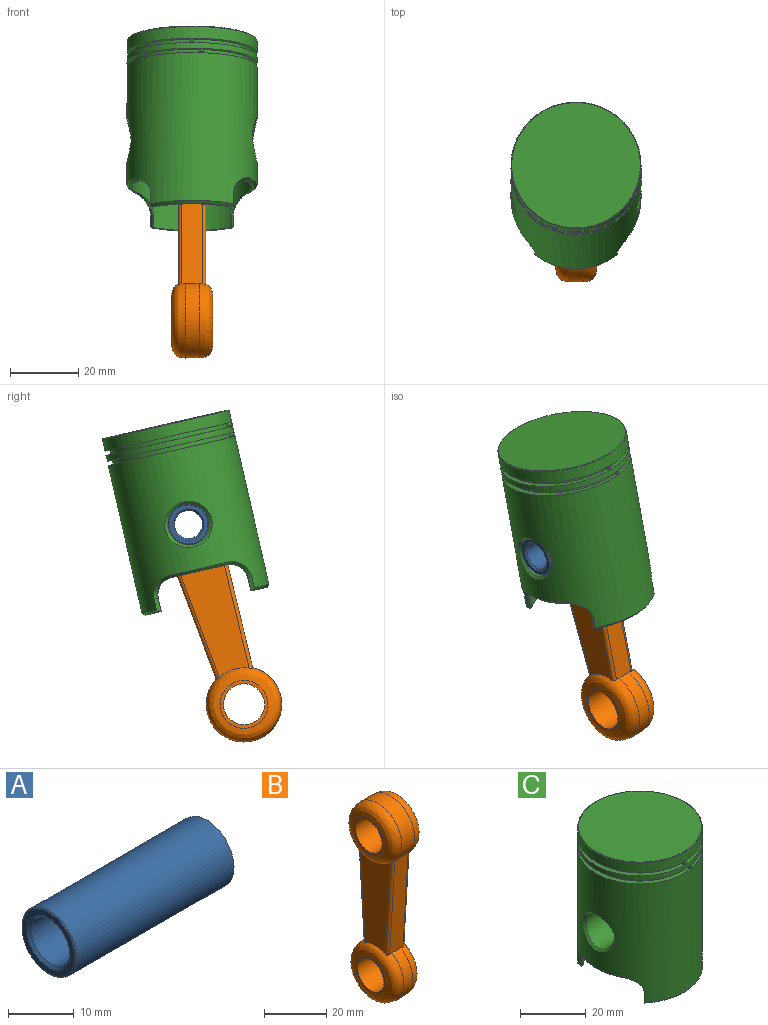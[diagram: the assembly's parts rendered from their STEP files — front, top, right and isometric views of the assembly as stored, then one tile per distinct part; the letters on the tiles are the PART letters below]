
ASSEMBLY  parts=3 mates=2
PART A: 6 faces, bbox 34x11.8x11.8 mm
  f0: cylinder r=4.1mm len=33.5mm, axis (1,0,0), area 863mm2, adj f2,f5
  f1: cylinder r=5.9mm len=33.8mm, axis (1,0,0), area 1253mm2, adj f2,f4
  f2: plane 11.8x11.8mm, normal (1,0,0), area 56.5mm2, adj f0,f1
  f3: plane 11.4x11.4mm, normal (-1,0,0), area 35.6mm2, adj f4,f5
  f4: cone r=5.9mm half-angle=45deg, axis (1,0,0), area 10.3mm2, adj f1,f3
  f5: cone r=4.6mm half-angle=45deg, axis (-1,0,0), area 19.3mm2, adj f0,f3
PART B: 21 faces, bbox 13.8x22x77 mm
  f0: cylinder r=6mm len=13.8mm, axis (1,0,0), area 520.2mm2, adj f2,f10
  f1: cylinder r=11mm len=22mm, axis (1,0,0), area 298.5mm2, adj f6,f7,f12,f13,f15
  f2: plane 14.01x14.01mm, normal (1,0,0), area 40.8mm2, adj f0,f15
  f3: cylinder r=11mm len=22mm, axis (1,0,0), area 229.8mm2, adj f6,f7,f14,f16
  f4: cylinder r=6mm len=12mm, axis (1,0,0), area 452.4mm2, adj f5,f9
  f5: plane 14.01x14.01mm, normal (1,0,0), area 40.8mm2, adj f4,f16
  f6: plane 37.97x6.04mm, normal (0,1,-0.06), area 227.7mm2, adj f1,f3,f12,f14,f15,f16,f18,f20
  f7: plane 37.97x6.04mm, normal (0,-1,-0.06), area 227.7mm2, adj f1,f3,f13,f14,f15,f16,f17,f19
  f8: plane 37.02x13.9mm, normal (1,0,0), area 392.3mm2, adj f15,f16,f19,f20
  f9: plane 14.01x14.01mm, normal (-1,0,0), area 40.9mm2, adj f4,f14
  f10: plane 14.01x14.01mm, normal (-1,0,0), area 40.8mm2, adj f0,f12
  f11: plane 37.02x13.9mm, normal (-1,0,0), area 392.3mm2, adj f12,f14,f17,f18
  f12: bspline ~21.99x21.98mm, area 374.1mm2, adj f1,f6,f10,f11,f13,f17,f18
  f13: bspline ~6.96x6.41mm, area 0mm2, adj f1,f7,f12
  f14: bspline ~21.99x21.98mm, area 369.7mm2, adj f3,f6,f7,f9,f11,f17,f18
  f15: bspline ~22x22mm, area 374.1mm2, adj f1,f2,f6,f7,f8,f19,f20
  f16: bspline ~22x22mm, area 369.7mm2, adj f3,f5,f6,f7,f8,f19,f20
  f17: cylinder r=1mm len=38.01mm, axis (0,0.06,-1), area 58.9mm2, adj f7,f11,f12,f14
  f18: cylinder r=1mm len=38.01mm, axis (0,0.06,1), area 58.9mm2, adj f6,f11,f12,f14
  f19: cylinder r=1mm len=38.01mm, axis (0,0.06,-1), area 58.9mm2, adj f7,f8,f15,f16
  f20: cylinder r=1mm len=38.01mm, axis (0,0.06,1), area 58.9mm2, adj f6,f8,f15,f16
PART C: 57 faces, bbox 38x38x53 mm
  f0: cylinder r=19mm len=38mm, axis (0,0,1), area 203.8mm2, adj f3,f7,f25
  f1: cylinder r=17.5mm len=35mm, axis (0,0,1), area 142.2mm2, adj f2,f3,f24
  f2: plane 38x38mm, normal (0,0,-1), area 171.9mm2, adj f1,f5,f24
  f3: plane 38x38mm, normal (0,0,1), area 172mm2, adj f0,f1
  f4: plane 37.6x37.6mm, normal (0,0,1), area 1110.4mm2, adj f52
  f5: cylinder r=19mm len=38mm, axis (0,0,1), area 418.6mm2, adj f2,f24,f52
  f6: cylinder r=17.5mm len=35mm, axis (0,0,1), area 142.1mm2, adj f7,f8,f25
  f7: plane 38x38mm, normal (0,0,-1), area 171.5mm2, adj f0,f6,f25
  f8: plane 38x38mm, normal (0,0,1), area 172mm2, adj f6,f23
  f9: plane 35x35mm, normal (0,0,-1), area 962.1mm2, adj f10
  f10: cylinder r=17.5mm len=43mm, axis (0,0,1), area 3596.7mm2, adj f9,f11,f12,f13,f14,f15,f16,f17
  f11: plane 23.72x4.9mm, normal (0,0,-1), area 20.3mm2, adj f10,f12,f22,f45,f47,f49
  f12: plane 4x0.41mm, normal (0,-1,0), area 1.6mm2, adj f10,f11,f13,f49
  f13: cylinder r=5mm len=5mm, axis (-1,0,0), area 5mm2, adj f10,f12,f14,f48
  f14: plane 16.8x2.95mm, normal (0,0,-1), area 14mm2, adj f10,f13,f15,f46
  f15: cylinder r=5mm len=5mm, axis (-1,0,0), area 5mm2, adj f10,f14,f16,f44
  f16: plane 4x0.41mm, normal (0,1,0), area 1.6mm2, adj f10,f15,f17,f42
  f17: plane 23.72x4.9mm, normal (0,0,-1), area 20.3mm2, adj f10,f16,f18,f38,f40,f42
  f18: plane 4x0.41mm, normal (0,1,0), area 1.6mm2, adj f10,f17,f19,f38
  f19: cylinder r=5mm len=5mm, axis (-1,0,0), area 5mm2, adj f10,f18,f20,f39
  f20: plane 16.8x2.95mm, normal (0,0,-1), area 14mm2, adj f10,f19,f21,f41
  f21: cylinder r=5mm len=5mm, axis (-1,0,0), area 5mm2, adj f10,f20,f22,f43
  f22: plane 4x0.41mm, normal (0,-1,0), area 1.6mm2, adj f10,f11,f21,f45
  f23: cylinder r=19mm len=44.3mm, axis (0,0,1), area 4430mm2, adj f8,f38,f39,f40,f41,f42,f43,f44
  f24: cylinder r=0.5mm len=1.5mm, axis (0,-1,0), area 4.6mm2, adj f1,f2,f5
  f25: cylinder r=0.52mm len=1.57mm, axis (0,-1,0), area 4.4mm2, adj f0,f6,f7
  f26: cylinder r=6mm len=12mm, axis (1,0,0), area 407.2mm2, adj f32,f51
  f27: cylinder r=6mm len=12mm, axis (1,0,0), area 407.2mm2, adj f37,f50
  f28: plane 15.8x7.09mm, normal (0,-1,0), area 108.8mm2, adj f10,f30,f31,f32,f53,f56
  f29: plane 15.8x7.09mm, normal (0,1,0), area 108.8mm2, adj f10,f30,f31,f32,f53,f56
  f30: plane 19.32x8.2mm, normal (0,0,1), area 140.4mm2, adj f10,f28,f29,f56
  f31: plane 19.32x8.2mm, normal (0,0,-1), area 140.4mm2, adj f10,f28,f29,f53
  f32: plane 19.32x12.2mm, normal (1,0,0), area 122.7mm2, adj f26,f28,f29,f53,f56
  f33: plane 19.32x8.2mm, normal (0,0,-1), area 140.4mm2, adj f10,f35,f36,f54
  f34: plane 19.32x8.2mm, normal (0,0,1), area 140.4mm2, adj f10,f35,f36,f55
  f35: plane 15.8x7.09mm, normal (0,-1,0), area 108.8mm2, adj f10,f33,f34,f37,f54,f55
  f36: plane 15.8x7.09mm, normal (0,1,0), area 108.8mm2, adj f10,f33,f34,f37,f54,f55
  f37: plane 19.32x12.2mm, normal (-1,0,0), area 122.7mm2, adj f27,f35,f36,f54,f55
  f38: plane 4.01x1.24mm, normal (-0.94,0.34,0), area 5mm2, adj f17,f18,f23,f39,f40
  f39: bspline ~6.24x5.7mm, area 11.6mm2, adj f19,f23,f38,f41
  f40: cone r=19mm half-angle=45deg, axis (0,0,1), area 25.8mm2, adj f17,f23,f38,f42
  f41: cone r=18.3mm half-angle=45deg, axis (0,0,1), area 17.6mm2, adj f20,f23,f39,f43
  f42: plane 4.01x1.24mm, normal (0.94,0.34,0), area 5mm2, adj f16,f17,f23,f40,f44
  f43: bspline ~6.24x5.7mm, area 11.6mm2, adj f21,f23,f41,f45
  f44: bspline ~6.24x5.7mm, area 11.6mm2, adj f15,f23,f42,f46
  f45: plane 4.01x1.24mm, normal (-0.94,-0.34,0), area 5mm2, adj f11,f22,f23,f43,f47
  f46: cone r=18.3mm half-angle=45deg, axis (0,0,1), area 17.6mm2, adj f14,f23,f44,f48
  f47: cone r=19mm half-angle=45deg, axis (0,0,1), area 25.8mm2, adj f11,f23,f45,f49
  f48: bspline ~6.24x5.7mm, area 11.6mm2, adj f13,f23,f46,f49
  f49: plane 4.01x1.24mm, normal (0.94,-0.34,0), area 5mm2, adj f11,f12,f23,f47,f48
  f50: bspline ~13.91x13.4mm, area 43.8mm2, adj f23,f27
  f51: bspline ~13.91x13.4mm, area 43.8mm2, adj f23,f26
  f52: cone r=18.8mm half-angle=45deg, axis (0,0,-1), area 33.6mm2, adj f4,f5
  f53: plane 19.32x1.8mm, normal (0.71,0,-0.71), area 49.2mm2, adj f28,f29,f31,f32
  f54: plane 19.32x1.8mm, normal (-0.71,0,-0.71), area 49.2mm2, adj f33,f35,f36,f37
  f55: plane 19.32x1.8mm, normal (-0.71,0,0.71), area 49.2mm2, adj f34,f35,f36,f37
  f56: plane 19.32x1.8mm, normal (0.71,0,0.71), area 49.2mm2, adj f28,f29,f30,f32
PLACE A rot(axis=(-1,0,0),12.9deg) t=(-74.95,-87.3,-9.13)mm
PLACE B rot(axis=(-1,0,0),17.2deg) t=(-74.25,-88.95,-8.68)mm
PLACE C rot(axis=(-1,0,0),12.9deg) t=(-74.31,-87.3,-9.13)mm
MATE revolute B.f0 <-> A.f0  axis (1,0,0) through (-67.35,-82.16,13.29)mm
MATE fastened C.f26 <-> A.f0  axis (1,0,0) through (-55.95,-82.16,13.29)mm
